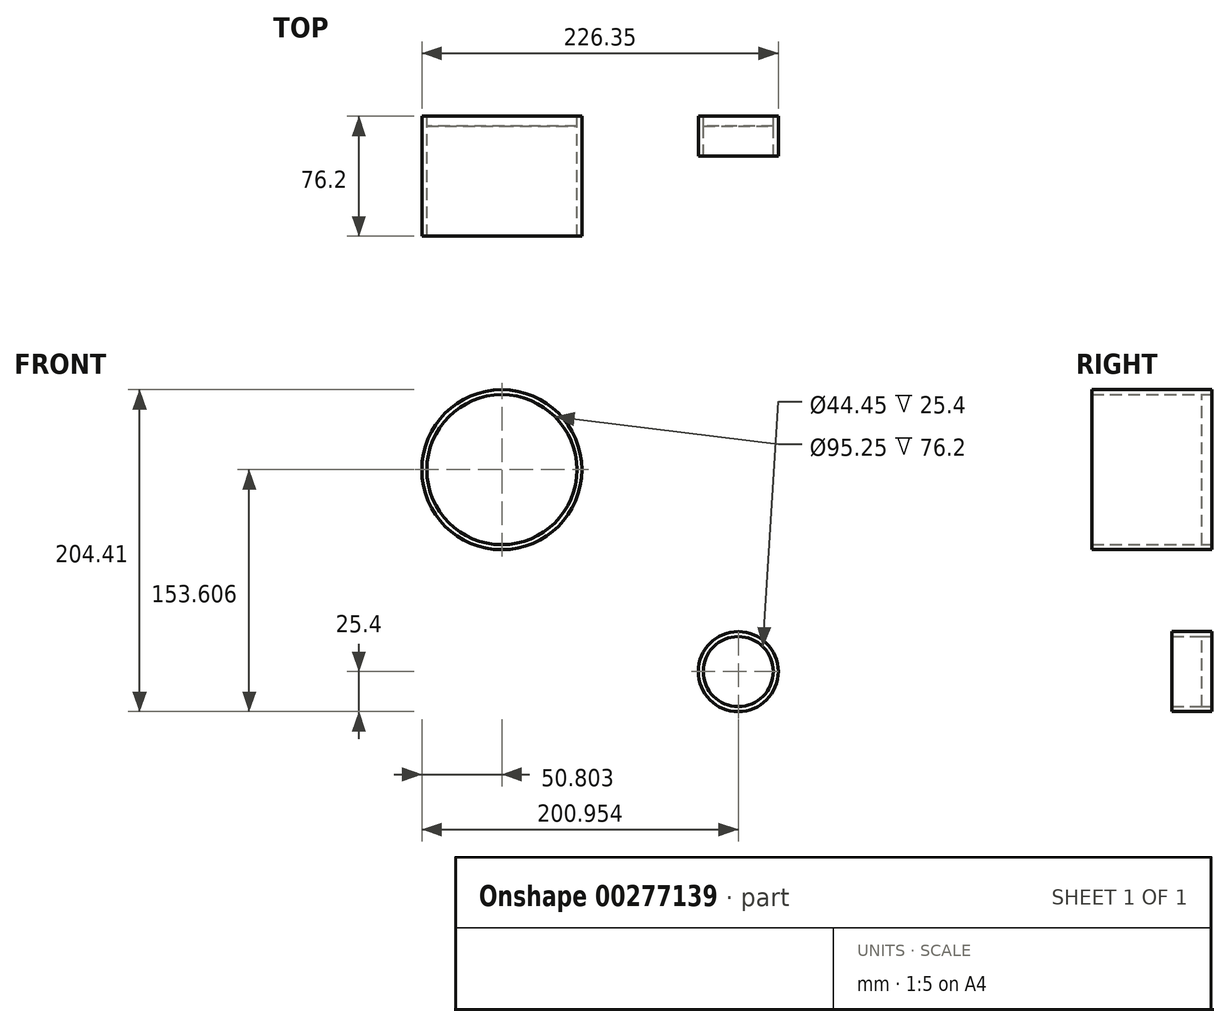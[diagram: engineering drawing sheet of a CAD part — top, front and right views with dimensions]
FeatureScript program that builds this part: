
annotation { "Feature Type Name" : "Feature", "Feature Type Description" : "" }
export const myFeature = defineFeature(function(context is Context, id is Id, definition is map)
    precondition{}
    {
        {
            var Q0;
            Q0=qCreatedBy(makeId("Front.planeOp"),FACE);
            var sketch = newSketch(context, id + "F0", { "sketchPlane" : qUnion([Q0])});
            skCircle(sketch, "E0", {"center": v(-84.82, 68.4) * mm, "radius": 47.63 * mm});
            skCircle(sketch, "E1", {"center": v(65.33, -59.8) * mm, "radius": 25.4 * mm});
            skCircle(sketch, "E2", {"center": v(65.33, -59.8) * mm, "radius": 22.23 * mm});
            skCircle(sketch, "E3", {"center": v(-84.82, 68.4) * mm, "radius": 50.8 * mm});
            skSolve(sketch);
        }
        {
            var Q0;
            Q0=makeQuery(id+"F0.imprint","IMPRINT",FACE,{"disambiguationData":[TD([[makeQuery(id+"F0.imprint","IMPRINT",EDGE,{"derivedFrom":sQuery(id+"F0.wireOp",EDGE,"E0")}),-1.0]])]});
            extrude(context, id + "F1", {"entities" : qUnion([Q0]), "depth" : 76.2 * mm});
        }
        {
            var Q0;
            Q0=makeQuery(id+"F0.imprint","IMPRINT",FACE,{"disambiguationData":[TD([[makeQuery(id+"F0.imprint","IMPRINT",EDGE,{"derivedFrom":sQuery(id+"F0.wireOp",EDGE,"E0")}),1.0]])]});
            extrude(context, id + "F2", {"entities" : qUnion([Q0]), "depth" : 6.35 * mm});
        }
        {
            var Q0;
            Q0=makeQuery(id+"F0.imprint","IMPRINT",FACE,{"disambiguationData":[TD([[makeQuery(id+"F0.imprint","IMPRINT",EDGE,{"derivedFrom":sQuery(id+"F0.wireOp",EDGE,"E2")}),1.0]])]});
            extrude(context, id + "F3", {"entities" : qUnion([Q0]), "depth" : 6.35 * mm});
        }
        {
            var Q0;
            Q0=makeQuery(id+"F0.imprint","IMPRINT",FACE,{"disambiguationData":[TD([[makeQuery(id+"F0.imprint","IMPRINT",EDGE,{"derivedFrom":sQuery(id+"F0.wireOp",EDGE,"E1")}),1.0]])]});
            extrude(context, id + "F4", {"entities" : qUnion([Q0]), "depth" : 25.4 * mm});
        }
    });
